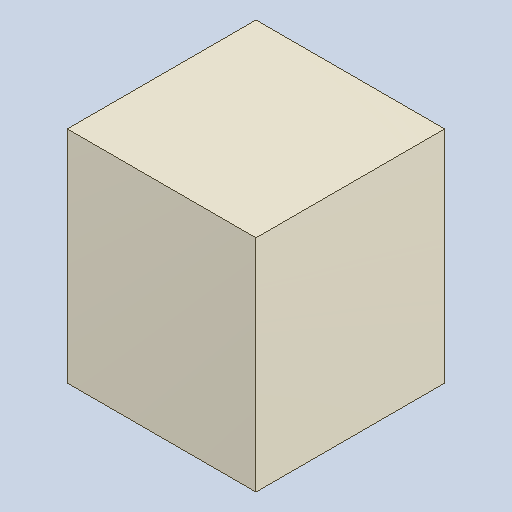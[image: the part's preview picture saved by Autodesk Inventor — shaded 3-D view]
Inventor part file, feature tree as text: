
AUTODESK INVENTOR PART (.ipt)
format: ipt  version: 2023.4 (Build 274418000, 418)  size: 82,944 bytes
history: native  units: mm
features: extrude x1
ambient origin geometry x8: Origin, YZ Plane, XZ Plane, XY Plane, X Axis, Y Axis, Z Axis, Center Point
bodies: Solid1 (feature_tree)
feature tree (1):
  extrude  "Extruded_8"  [1 undecoded]
note: 1 required parameter value undecoded (feature->parameter linkage not recoverable at this tier; creation-order binding heuristic only, values carry confidence <= 0.55)
